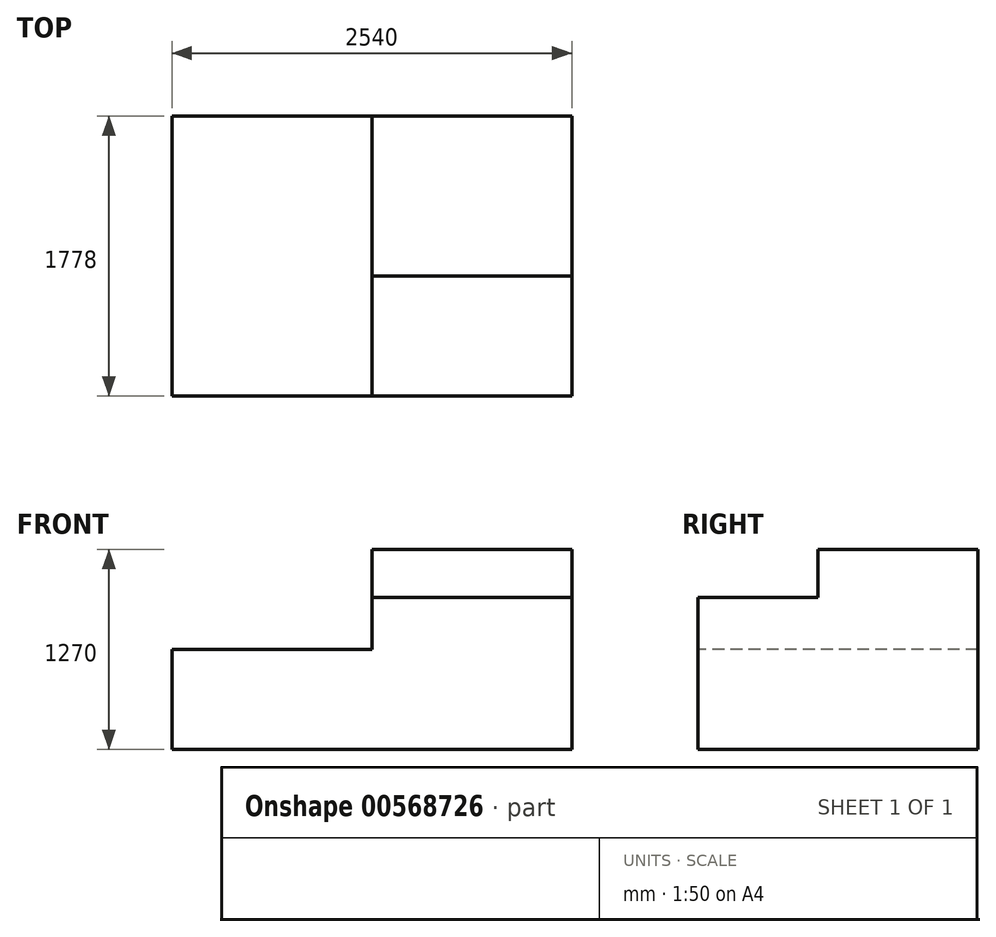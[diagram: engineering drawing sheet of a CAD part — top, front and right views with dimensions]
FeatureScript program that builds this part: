
annotation { "Feature Type Name" : "Feature", "Feature Type Description" : "" }
export const myFeature = defineFeature(function(context is Context, id is Id, definition is map)
    precondition{}
    {
        {
            var Q0;
            Q0=qCreatedBy(makeId("Front.planeOp"),FACE);
            var sketch = newSketch(context, id + "F0", { "sketchPlane" : qUnion([Q0])});
            skLineSegment(sketch, "E0.bottom", {"start": v(0, 0) * mm, "end": v(2540, 0) * mm});
            skLineSegment(sketch, "E0.top", {"start": v(0, 1270) * mm, "end": v(2540, 1270) * mm});
            skLineSegment(sketch, "E0.left", {"start": v(0, 0) * mm, "end": v(0, 1270) * mm});
            skLineSegment(sketch, "E0.right", {"start": v(2540, 0) * mm, "end": v(2540, 1270) * mm});
            skSolve(sketch);
        }
        {
            var Q0;
            Q0=makeQuery(id+"F0.imprint","IMPRINT",FACE,{"disambiguationData":[TD([[makeQuery(id+"F0.imprint","IMPRINT",EDGE,{"derivedFrom":sQuery(id+"F0.wireOp",EDGE,"E0.bottom")}),1.0]])]});
            extrude(context, id + "F1", {"entities" : qUnion([Q0]), "depth" : 1778 * mm, "offsetDistance" : 25.4 * mm});
        }
        {
            var Q0;
            Q0=makeQuery(id+"F1.opExtrude","CAP_FACE",FACE,{"disambiguationData":[OSD([sQuery(id+"F0.wireOp",EDGE,"E0.bottom"),sQuery(id+"F0.wireOp",EDGE,"E0.top"),sQuery(id+"F0.wireOp",EDGE,"E0.left"),sQuery(id+"F0.wireOp",EDGE,"E0.right")])],"isStart":false});
            var sketch = newSketch(context, id + "F2", { "sketchPlane" : qUnion([Q0])});
            skLineSegment(sketch, "E1.bottom", {"start": v(0, 1270) * mm, "end": v(1270, 1270) * mm});
            skLineSegment(sketch, "E1.top", {"start": v(0, 635) * mm, "end": v(1270, 635) * mm});
            skLineSegment(sketch, "E1.left", {"start": v(0, 1270) * mm, "end": v(0, 635) * mm});
            skLineSegment(sketch, "E1.right", {"start": v(1270, 1270) * mm, "end": v(1270, 635) * mm});
            skSolve(sketch);
        }
        {
            var Q0;
            Q0=makeQuery(id+"F2.imprint","IMPRINT",FACE,{"disambiguationData":[TD([[makeQuery(id+"F2.imprint","IMPRINT",EDGE,{"derivedFrom":sQuery(id+"F2.wireOp",EDGE,"E1.bottom")}),-1.0]])]});
            extrude(context, id + "F3", {"entities" : qUnion([Q0]), "operationType" : NewBodyOperationType.REMOVE, "endBound" : BoundingType.THROUGH_ALL, "oppositeDirection" : true, "depth" : 25.4 * mm, "offsetDistance" : 25.4 * mm});
        }
        {
            var Q0;
            Q0=makeQuery(id+"F3.boolean.opBoolean","COPY",FACE,{"derivedFrom":makeQuery(id+"F3.opExtrude","SWEPT_FACE",FACE,{"disambiguationData":[OSD([sQuery(id+"F2.wireOp",EDGE,"E1.right")])]})});
            var sketch = newSketch(context, id + "F4", { "sketchPlane" : qUnion([Q0])});
            skLineSegment(sketch, "E2.bottom", {"start": v(1778, 1270) * mm, "end": v(1016, 1270) * mm});
            skLineSegment(sketch, "E2.top", {"start": v(1778, 965.2) * mm, "end": v(1016, 965.2) * mm});
            skLineSegment(sketch, "E2.left", {"start": v(1778, 1270) * mm, "end": v(1778, 965.2) * mm});
            skLineSegment(sketch, "E2.right", {"start": v(1016, 1270) * mm, "end": v(1016, 965.2) * mm});
            skSolve(sketch);
        }
        {
            var Q0;
            Q0=makeQuery(id+"F4.imprint","IMPRINT",FACE,{"disambiguationData":[TD([[makeQuery(id+"F4.imprint","IMPRINT",EDGE,{"derivedFrom":sQuery(id+"F4.wireOp",EDGE,"E2.bottom")}),-1.0]])]});
            extrude(context, id + "F5", {"entities" : qUnion([Q0]), "operationType" : NewBodyOperationType.REMOVE, "endBound" : BoundingType.THROUGH_ALL, "oppositeDirection" : true, "depth" : 25.4 * mm, "offsetDistance" : 25.4 * mm});
        }
    });
